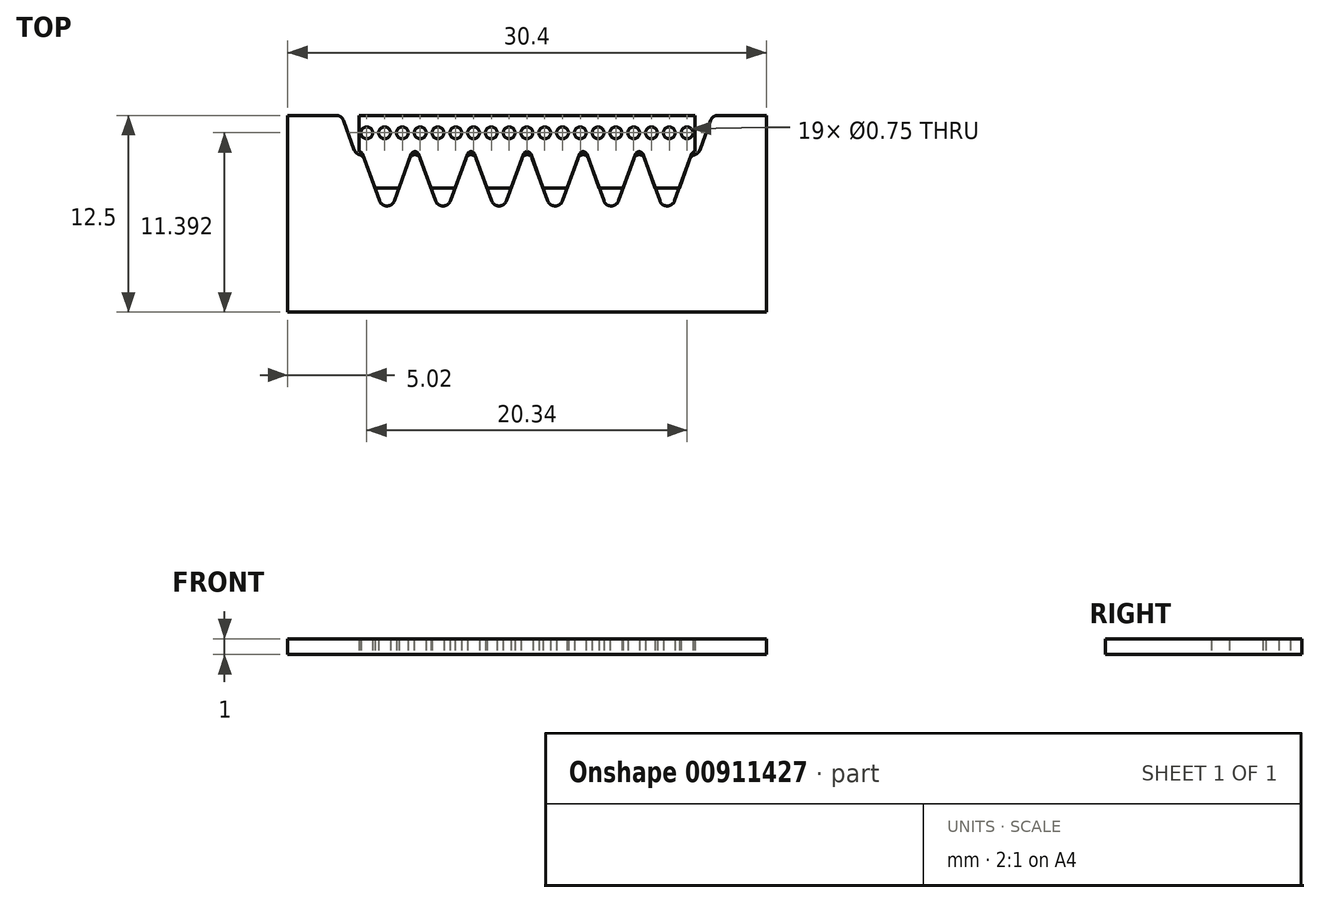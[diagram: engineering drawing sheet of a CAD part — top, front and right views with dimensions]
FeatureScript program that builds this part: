
annotation { "Feature Type Name" : "Feature", "Feature Type Description" : "" }
export const myFeature = defineFeature(function(context is Context, id is Id, definition is map)
    precondition{}
    {
        {
            var Q0;
            Q0=qCreatedBy(makeId("Top.planeOp"),FACE);
            var sketch = newSketch(context, id + "F0", { "sketchPlane" : qUnion([Q0])});
            skLineSegment(sketch, "E0", {"start": v(0.23, 70.03) * mm, "end": v(1.01, 67.9) * mm});
            skLineSegment(sketch, "E1", {"start": v(1.01, 67.9) * mm, "end": v(2.55, 67.9) * mm});
            skLineSegment(sketch, "E2", {"start": v(2.55, 67.9) * mm, "end": v(3.33, 70.03) * mm});
            skLineSegment(sketch, "E3", {"start": v(0, 70.2) * mm, "end": v(0, 70.2) * mm});
            skLineSegment(sketch, "E4", {"start": v(0, 70.2) * mm, "end": v(0, 72.5) * mm});
            skLineSegment(sketch, "E5", {"start": v(0, 72.5) * mm, "end": v(21.36, 72.5) * mm});
            skLineSegment(sketch, "E6", {"start": v(21.36, 72.5) * mm, "end": v(21.36, 70.2) * mm});
            skLineSegment(sketch, "E7", {"start": v(3.8, 70.03) * mm, "end": v(4.57, 67.9) * mm});
            skLineSegment(sketch, "E8", {"start": v(4.57, 67.9) * mm, "end": v(6.1, 67.9) * mm});
            skLineSegment(sketch, "E9", {"start": v(6.1, 67.9) * mm, "end": v(6.89, 70.03) * mm});
            skLineSegment(sketch, "E10", {"start": v(7.35, 70.03) * mm, "end": v(8.13, 67.9) * mm});
            skLineSegment(sketch, "E11", {"start": v(8.13, 67.9) * mm, "end": v(9.67, 67.9) * mm});
            skLineSegment(sketch, "E12", {"start": v(9.67, 67.9) * mm, "end": v(10.45, 70.03) * mm});
            skLineSegment(sketch, "E13", {"start": v(10.91, 70.03) * mm, "end": v(11.7, 67.9) * mm});
            skLineSegment(sketch, "E14", {"start": v(11.7, 67.9) * mm, "end": v(13.23, 67.9) * mm});
            skLineSegment(sketch, "E15", {"start": v(13.23, 67.9) * mm, "end": v(14, 70.03) * mm});
            skLineSegment(sketch, "E16", {"start": v(14.47, 70.03) * mm, "end": v(15.25, 67.9) * mm});
            skLineSegment(sketch, "E17", {"start": v(15.25, 67.9) * mm, "end": v(16.79, 67.9) * mm});
            skLineSegment(sketch, "E18", {"start": v(16.79, 67.9) * mm, "end": v(17.57, 70.03) * mm});
            skLineSegment(sketch, "E19", {"start": v(18.03, 70.03) * mm, "end": v(18.81, 67.9) * mm});
            skLineSegment(sketch, "E20", {"start": v(18.81, 67.9) * mm, "end": v(20.35, 67.9) * mm});
            skLineSegment(sketch, "E21", {"start": v(20.35, 67.9) * mm, "end": v(21.13, 70.03) * mm});
            skPoint(sketch, "E22.visualSharp", {"position": v(3.56, 70.67) * mm});
            skArc(sketch, "E22.filletArc", {"start": v(3.8, 70.03) * mm, "mid": v(3.56, 70.2) * mm, "end": v(3.33, 70.03) * mm});
            skLineSegment(sketch, "E23", {"start": v(4.16, 67.9) * mm, "end": v(21.14, 67.9) * mm, "construction": true});
            skPoint(sketch, "E24.visualSharp", {"position": v(7.12, 70.67) * mm});
            skArc(sketch, "E24.filletArc", {"start": v(7.35, 70.03) * mm, "mid": v(7.12, 70.2) * mm, "end": v(6.89, 70.03) * mm});
            skPoint(sketch, "E25.visualSharp", {"position": v(14.24, 70.67) * mm});
            skArc(sketch, "E25.filletArc", {"start": v(14.47, 70.03) * mm, "mid": v(14.24, 70.2) * mm, "end": v(14, 70.03) * mm});
            skArc(sketch, "E26.filletArc", {"start": v(18.03, 70.03) * mm, "mid": v(17.8, 70.2) * mm, "end": v(17.57, 70.03) * mm});
            skLineSegment(sketch, "E27", {"start": v(21.36, 70.2) * mm, "end": v(21.36, 70.2) * mm});
            skPoint(sketch, "E28.visualSharp", {"position": v(10.68, 70.67) * mm});
            skArc(sketch, "E28.filletArc", {"start": v(10.91, 70.03) * mm, "mid": v(10.68, 70.2) * mm, "end": v(10.45, 70.03) * mm});
            skLineSegment(sketch, "E29", {"start": v(10.68, 34.44) * mm, "end": v(10.68, 52.4) * mm, "construction": true});
            skArc(sketch, "E30.filletArc", {"start": v(0.23, 70.03) * mm, "mid": v(0.14, 70.15) * mm, "end": v(0, 70.2) * mm});
            skArc(sketch, "E31.filletArc", {"start": v(21.36, 70.2) * mm, "mid": v(21.22, 70.15) * mm, "end": v(21.13, 70.03) * mm});
            skLineSegment(sketch, "E32", {"start": v(0, 71.4) * mm, "end": v(21.36, 71.4) * mm, "construction": true});
            skPoint(sketch, "E32.endSnap0", {"position": v(21.36, 71.34) * mm});
            skLineSegment(sketch, "E33", {"start": v(0.36, 69.7) * mm, "end": v(1.31, 67.07) * mm});
            skLineSegment(sketch, "E34", {"start": v(2.25, 67.07) * mm, "end": v(3.23, 69.77) * mm});
            skLineSegment(sketch, "E35", {"start": v(3.89, 69.77) * mm, "end": v(4.87, 67.07) * mm});
            skLineSegment(sketch, "E36", {"start": v(5.8, 67.07) * mm, "end": v(6.8, 69.77) * mm});
            skLineSegment(sketch, "E37", {"start": v(7.45, 69.77) * mm, "end": v(8.43, 67.07) * mm});
            skLineSegment(sketch, "E38", {"start": v(9.37, 67.07) * mm, "end": v(10.35, 69.77) * mm});
            skLineSegment(sketch, "E39", {"start": v(11, 69.77) * mm, "end": v(12, 67.07) * mm});
            skLineSegment(sketch, "E40", {"start": v(12.93, 67.07) * mm, "end": v(13.91, 69.77) * mm});
            skLineSegment(sketch, "E41", {"start": v(14.57, 69.77) * mm, "end": v(15.55, 67.07) * mm});
            skLineSegment(sketch, "E42", {"start": v(16.49, 67.07) * mm, "end": v(17.47, 69.77) * mm});
            skLineSegment(sketch, "E43", {"start": v(18.13, 69.77) * mm, "end": v(19.11, 67.07) * mm});
            skLineSegment(sketch, "E44", {"start": v(20.05, 67.07) * mm, "end": v(21, 69.7) * mm});
            skArc(sketch, "E45.filletArc", {"start": v(1.31, 67.07) * mm, "mid": v(1.78, 66.74) * mm, "end": v(2.25, 67.07) * mm});
            skArc(sketch, "E46.filletArc", {"start": v(4.87, 67.07) * mm, "mid": v(5.34, 66.74) * mm, "end": v(5.8, 67.07) * mm});
            skArc(sketch, "E47.filletArc", {"start": v(8.43, 67.07) * mm, "mid": v(8.9, 66.74) * mm, "end": v(9.37, 67.07) * mm});
            skArc(sketch, "E48.filletArc", {"start": v(12, 67.07) * mm, "mid": v(12.46, 66.74) * mm, "end": v(12.93, 67.07) * mm});
            skArc(sketch, "E49.filletArc", {"start": v(15.55, 67.07) * mm, "mid": v(16.02, 66.74) * mm, "end": v(16.49, 67.07) * mm});
            skArc(sketch, "E50.filletArc", {"start": v(19.11, 67.07) * mm, "mid": v(19.58, 66.74) * mm, "end": v(20.05, 67.07) * mm});
            skArc(sketch, "E51.filletArc", {"start": v(18.13, 69.77) * mm, "mid": v(17.8, 70) * mm, "end": v(17.47, 69.77) * mm});
            skArc(sketch, "E52.filletArc", {"start": v(14.57, 69.77) * mm, "mid": v(14.24, 70) * mm, "end": v(13.91, 69.77) * mm});
            skArc(sketch, "E53.filletArc", {"start": v(11, 69.77) * mm, "mid": v(10.68, 70) * mm, "end": v(10.35, 69.77) * mm});
            skArc(sketch, "E54.filletArc", {"start": v(7.45, 69.77) * mm, "mid": v(7.12, 70) * mm, "end": v(6.8, 69.77) * mm});
            skArc(sketch, "E55.filletArc", {"start": v(3.89, 69.77) * mm, "mid": v(3.56, 70) * mm, "end": v(3.23, 69.77) * mm});
            skLineSegment(sketch, "E56", {"start": v(0, 66.74) * mm, "end": v(21.8, 66.74) * mm, "construction": true});
            skPoint(sketch, "E56.startSnap0", {"position": v(1.78, 66.74) * mm});
            skLineSegment(sketch, "E57", {"start": v(2.94, 70) * mm, "end": v(18.52, 70) * mm, "construction": true});
            skPoint(sketch, "E57.startSnap0", {"position": v(3.56, 70) * mm});
            skLineSegment(sketch, "E58", {"start": v(-1.44, 72.5) * mm, "end": v(-4.52, 72.5) * mm});
            skLineSegment(sketch, "E59", {"start": v(-4.52, 72.5) * mm, "end": v(-4.52, 60) * mm});
            skLineSegment(sketch, "E60", {"start": v(-4.52, 60) * mm, "end": v(25.88, 60) * mm});
            skLineSegment(sketch, "E61", {"start": v(25.88, 60) * mm, "end": v(25.88, 72.5) * mm});
            skLineSegment(sketch, "E62", {"start": v(25.88, 72.5) * mm, "end": v(22.8, 72.5) * mm});
            skLineSegment(sketch, "E63", {"start": v(22.33, 72.17) * mm, "end": v(21.65, 70.3) * mm});
            skLineSegment(sketch, "E64", {"start": v(-0.3, 70.3) * mm, "end": v(-0.97, 72.17) * mm});
            skArc(sketch, "E65.filletArc", {"start": v(0.36, 69.7) * mm, "mid": v(0.23, 69.88) * mm, "end": v(0.03, 70) * mm});
            skArc(sketch, "E66.filletArc", {"start": v(-0.3, 70.3) * mm, "mid": v(-0.17, 70.12) * mm, "end": v(0.03, 70) * mm});
            skArc(sketch, "E67.filletArc", {"start": v(21.33, 70) * mm, "mid": v(21.13, 69.88) * mm, "end": v(21, 69.7) * mm});
            skArc(sketch, "E68.filletArc", {"start": v(21.33, 70) * mm, "mid": v(21.53, 70.12) * mm, "end": v(21.65, 70.3) * mm});
            skPoint(sketch, "E69.visualSharp", {"position": v(22.45, 72.5) * mm});
            skArc(sketch, "E69.filletArc", {"start": v(22.8, 72.5) * mm, "mid": v(22.51, 72.4) * mm, "end": v(22.33, 72.17) * mm});
            skArc(sketch, "E70.filletArc", {"start": v(-0.97, 72.17) * mm, "mid": v(-1.15, 72.4) * mm, "end": v(-1.44, 72.5) * mm});
            skLineSegment(sketch, "E71", {"start": v(-17.3, 0) * mm, "end": v(33.13, 0) * mm, "construction": true});
            skCircle(sketch, "E72", {"center": v(0.5, 71.4) * mm, "radius": 0.38 * mm});
            skCircle(sketch, "E73.1.0.0", {"center": v(1.63, 71.4) * mm, "radius": 0.38 * mm});
            skCircle(sketch, "E73.2.0.0", {"center": v(2.76, 71.4) * mm, "radius": 0.38 * mm});
            skCircle(sketch, "E73.3.0.0", {"center": v(3.89, 71.4) * mm, "radius": 0.38 * mm});
            skCircle(sketch, "E73.4.0.0", {"center": v(5.02, 71.4) * mm, "radius": 0.38 * mm});
            skCircle(sketch, "E73.5.0.0", {"center": v(6.15, 71.4) * mm, "radius": 0.38 * mm});
            skCircle(sketch, "E73.6.0.0", {"center": v(7.28, 71.4) * mm, "radius": 0.38 * mm});
            skCircle(sketch, "E73.7.0.0", {"center": v(8.4, 71.4) * mm, "radius": 0.38 * mm});
            skCircle(sketch, "E73.8.0.0", {"center": v(9.54, 71.4) * mm, "radius": 0.38 * mm});
            skCircle(sketch, "E73.9.0.0", {"center": v(10.67, 71.4) * mm, "radius": 0.38 * mm});
            skCircle(sketch, "E73.10.0.0", {"center": v(11.8, 71.4) * mm, "radius": 0.38 * mm});
            skCircle(sketch, "E73.11.0.0", {"center": v(12.93, 71.4) * mm, "radius": 0.38 * mm});
            skCircle(sketch, "E73.12.0.0", {"center": v(14.06, 71.4) * mm, "radius": 0.38 * mm});
            skCircle(sketch, "E73.13.0.0", {"center": v(15.19, 71.4) * mm, "radius": 0.38 * mm});
            skCircle(sketch, "E73.14.0.0", {"center": v(16.32, 71.4) * mm, "radius": 0.38 * mm});
            skCircle(sketch, "E73.15.0.0", {"center": v(17.45, 71.4) * mm, "radius": 0.38 * mm});
            skCircle(sketch, "E73.16.0.0", {"center": v(18.58, 71.4) * mm, "radius": 0.38 * mm});
            skCircle(sketch, "E73.17.0.0", {"center": v(19.7, 71.4) * mm, "radius": 0.38 * mm});
            skCircle(sketch, "E73.18.0.0", {"center": v(20.84, 71.4) * mm, "radius": 0.38 * mm});
            skLineSegment(sketch, "E73.direction1", {"start": v(0.5, 71.4) * mm, "end": v(1.63, 71.4) * mm, "construction": true});
            skSolve(sketch);
        }
        {
            var Q0;
            Q0=makeQuery(id+"F0.imprint","IMPRINT",FACE,{"disambiguationData":[TD([[makeQuery(id+"F0.imprint","IMPRINT",EDGE,{"derivedFrom":sQuery(id+"F0.wireOp",EDGE,"E0")}),1.0]])]});
            extrude(context, id + "F1", {"entities" : qUnion([Q0]), "depth" : 1 * mm, "offsetDistance" : 25 * mm});
        }
        {
            var Q0;
            {var subQ12=sQuery(id+"F0.wireOp",EDGE,"E45.filletArc");Q0=makeQuery(id+"F0.imprint","IMPRINT",FACE,{"disambiguationData":[TD([[makeQuery(id+"F0.imprint","IMPRINT",EDGE,{"derivedFrom":subQ12}),-1.0]])]});}
            extrude(context, id + "F2", {"entities" : qUnion([Q0]), "depth" : 1 * mm, "offsetDistance" : 25 * mm});
        }
        {
            var Q0;
            Q0=makeQuery(id+"F0.imprint","IMPRINT",FACE,{"disambiguationData":[TD([[makeQuery(id+"F0.imprint","IMPRINT",EDGE,{"derivedFrom":sQuery(id+"F0.wireOp",EDGE,"E72")}),1.0]])]});
            var Q1;
            Q1=makeQuery(id+"F0.imprint","IMPRINT",FACE,{"disambiguationData":[TD([[makeQuery(id+"F0.imprint","IMPRINT",EDGE,{"derivedFrom":sQuery(id+"F0.wireOp",EDGE,"E73.1.0.0")}),1.0]])]});
            var Q2;
            Q2=makeQuery(id+"F0.imprint","IMPRINT",FACE,{"disambiguationData":[TD([[makeQuery(id+"F0.imprint","IMPRINT",EDGE,{"derivedFrom":sQuery(id+"F0.wireOp",EDGE,"E73.2.0.0")}),1.0]])]});
            var Q3;
            Q3=makeQuery(id+"F0.imprint","IMPRINT",FACE,{"disambiguationData":[TD([[makeQuery(id+"F0.imprint","IMPRINT",EDGE,{"derivedFrom":sQuery(id+"F0.wireOp",EDGE,"E73.3.0.0")}),1.0]])]});
            var Q4;
            Q4=makeQuery(id+"F0.imprint","IMPRINT",FACE,{"disambiguationData":[TD([[makeQuery(id+"F0.imprint","IMPRINT",EDGE,{"derivedFrom":sQuery(id+"F0.wireOp",EDGE,"E73.4.0.0")}),1.0]])]});
            var Q5;
            Q5=makeQuery(id+"F0.imprint","IMPRINT",FACE,{"disambiguationData":[TD([[makeQuery(id+"F0.imprint","IMPRINT",EDGE,{"derivedFrom":sQuery(id+"F0.wireOp",EDGE,"E73.5.0.0")}),1.0]])]});
            var Q6;
            Q6=makeQuery(id+"F0.imprint","IMPRINT",FACE,{"disambiguationData":[TD([[makeQuery(id+"F0.imprint","IMPRINT",EDGE,{"derivedFrom":sQuery(id+"F0.wireOp",EDGE,"E73.6.0.0")}),1.0]])]});
            var Q7;
            Q7=makeQuery(id+"F0.imprint","IMPRINT",FACE,{"disambiguationData":[TD([[makeQuery(id+"F0.imprint","IMPRINT",EDGE,{"derivedFrom":sQuery(id+"F0.wireOp",EDGE,"E73.7.0.0")}),1.0]])]});
            var Q8;
            Q8=makeQuery(id+"F0.imprint","IMPRINT",FACE,{"disambiguationData":[TD([[makeQuery(id+"F0.imprint","IMPRINT",EDGE,{"derivedFrom":sQuery(id+"F0.wireOp",EDGE,"E73.8.0.0")}),1.0]])]});
            var Q9;
            Q9=makeQuery(id+"F0.imprint","IMPRINT",FACE,{"disambiguationData":[TD([[makeQuery(id+"F0.imprint","IMPRINT",EDGE,{"derivedFrom":sQuery(id+"F0.wireOp",EDGE,"E73.9.0.0")}),1.0]])]});
            var Q10;
            Q10=makeQuery(id+"F0.imprint","IMPRINT",FACE,{"disambiguationData":[TD([[makeQuery(id+"F0.imprint","IMPRINT",EDGE,{"derivedFrom":sQuery(id+"F0.wireOp",EDGE,"E73.10.0.0")}),1.0]])]});
            var Q11;
            Q11=makeQuery(id+"F0.imprint","IMPRINT",FACE,{"disambiguationData":[TD([[makeQuery(id+"F0.imprint","IMPRINT",EDGE,{"derivedFrom":sQuery(id+"F0.wireOp",EDGE,"E73.11.0.0")}),1.0]])]});
            var Q12;
            Q12=makeQuery(id+"F0.imprint","IMPRINT",FACE,{"disambiguationData":[TD([[makeQuery(id+"F0.imprint","IMPRINT",EDGE,{"derivedFrom":sQuery(id+"F0.wireOp",EDGE,"E73.12.0.0")}),1.0]])]});
            var Q13;
            Q13=makeQuery(id+"F0.imprint","IMPRINT",FACE,{"disambiguationData":[TD([[makeQuery(id+"F0.imprint","IMPRINT",EDGE,{"derivedFrom":sQuery(id+"F0.wireOp",EDGE,"E73.15.0.0")}),1.0]])]});
            var Q14;
            Q14=makeQuery(id+"F0.imprint","IMPRINT",FACE,{"disambiguationData":[TD([[makeQuery(id+"F0.imprint","IMPRINT",EDGE,{"derivedFrom":sQuery(id+"F0.wireOp",EDGE,"E73.16.0.0")}),1.0]])]});
            var Q15;
            Q15=makeQuery(id+"F0.imprint","IMPRINT",FACE,{"disambiguationData":[TD([[makeQuery(id+"F0.imprint","IMPRINT",EDGE,{"derivedFrom":sQuery(id+"F0.wireOp",EDGE,"E73.17.0.0")}),1.0]])]});
            var Q16;
            Q16=makeQuery(id+"F0.imprint","IMPRINT",FACE,{"disambiguationData":[TD([[makeQuery(id+"F0.imprint","IMPRINT",EDGE,{"derivedFrom":sQuery(id+"F0.wireOp",EDGE,"E73.18.0.0")}),1.0]])]});
            var Q17;
            Q17=makeQuery(id+"F0.imprint","IMPRINT",FACE,{"disambiguationData":[TD([[makeQuery(id+"F0.imprint","IMPRINT",EDGE,{"derivedFrom":sQuery(id+"F0.wireOp",EDGE,"E73.14.0.0")}),1.0]])]});
            var Q18;
            Q18=makeQuery(id+"F0.imprint","IMPRINT",FACE,{"disambiguationData":[TD([[makeQuery(id+"F0.imprint","IMPRINT",EDGE,{"derivedFrom":sQuery(id+"F0.wireOp",EDGE,"E73.13.0.0")}),1.0]])]});
            extrude(context, id + "F3", {"entities" : qUnion([Q0, Q1, Q2, Q3, Q4, Q5, Q6, Q7, Q8, Q9, Q10, Q11, Q12, Q13, Q14, Q15, Q16, Q17, Q18]), "depth" : 1 * mm, "offsetDistance" : 25 * mm});
        }
    });
